# Revit family: Access_Door-Insulated-Best Access Doors-All_Surface_Types-BA-FRI-HS
name_source: partatom
category: Specialty Equipment
revit_build: Autodesk Revit 2017 (Build: 20160225_1515(x64)
units: mm (PartAtom-declared; Revit-internal decimal feet)

## family parameters
Cut with Voids When Loaded = No
Host = Face
OmniClass Number = 23.30.10.27.17
Part Type = Normal
Room Calculation Point = No
Round Connector Dimension = Use Diameter
Shared = No

## types (1)
- Not a Type - Load Type Catalog
    Assembly Code = C1020700
    Ceiling Constraint = Maximum dimensions for ceiling mounted panels are 24W x 36H.
    Ceiling Mounted = No
    Construction Material = Metal - Best Access Doors - Aluminum
    Default Elevation = 0"
    Description = Fire Rated Insulated Access Door for All Surface Types
    Door Height = 24"
    Door Height Calc = 24"
    Door Width = 24"
    Door Width Calc = 24"
    Finish = Metal - Best Access Doors - Powder Coated White
    Height Actual = 26"
    Manufacturer = Best Access Doors
    Model = BA-FRI-HS
    Product data url = https://bimobject.com
    URL = https://www.bestaccessdoors.com
    Wall Mounted = Yes
    Width Actual = 26"

## geometry (parser evidence)
native form markers: Blend x4, Sweep x13
no freeform markers — native parametric forms only
